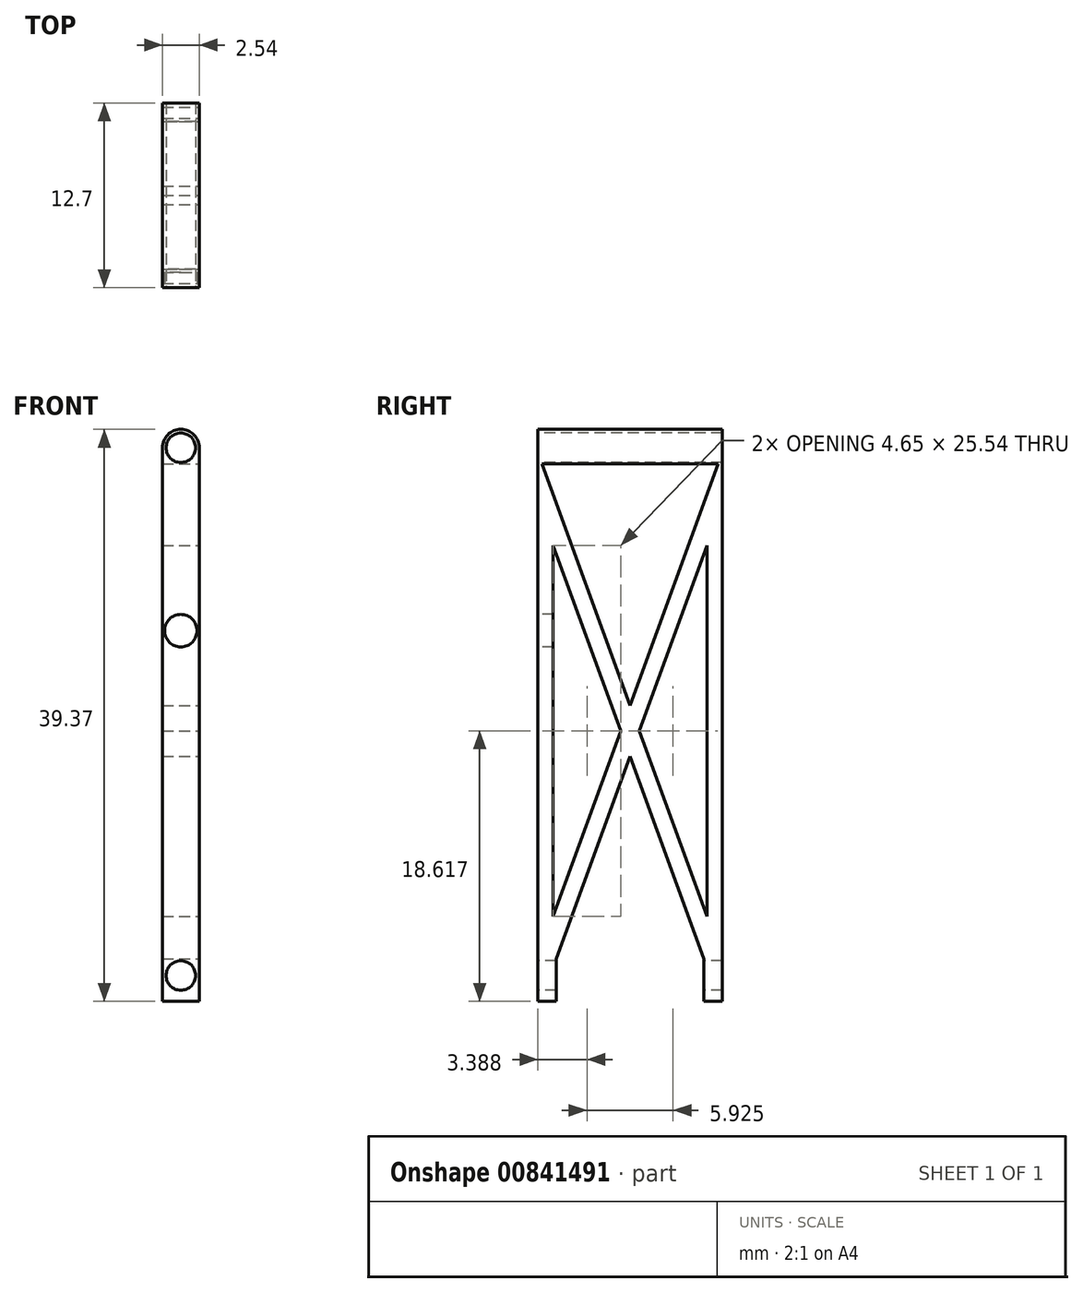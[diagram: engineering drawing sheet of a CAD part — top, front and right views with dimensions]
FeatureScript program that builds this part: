
annotation { "Feature Type Name" : "Feature", "Feature Type Description" : "" }
export const myFeature = defineFeature(function(context is Context, id is Id, definition is map)
    precondition{}
    {
        {
            var Q0;
            Q0=qCreatedBy(makeId("Front.planeOp"),FACE);
            var sketch = newSketch(context, id + "F0", { "sketchPlane" : qUnion([Q0])});
            skArc(sketch, "E0", {"start": v(1.27, 0) * mm, "mid": v(0.9, 0.9) * mm, "end": v(0, 1.27) * mm});
            skArc(sketch, "E1.MirrorCS", {"start": v(-1.27, 0) * mm, "mid": v(-0.9, 0.9) * mm, "end": v(0, 1.27) * mm});
            skLineSegment(sketch, "E2", {"start": v(-1.27, 0) * mm, "end": v(-1.27, -38.1) * mm});
            skLineSegment(sketch, "E3", {"start": v(1.27, 0) * mm, "end": v(1.27, -38.1) * mm});
            skLineSegment(sketch, "E4", {"start": v(-1.27, -38.1) * mm, "end": v(1.27, -38.1) * mm});
            skSolve(sketch);
        }
        {
            var Q0;
            Q0 = qSketchRegion(id + "F0", true);
            extrude(context, id + "F1", {"entities" : qUnion([Q0]), "endBound" : BoundingType.SYMMETRIC, "depth" : 12.7 * mm, "offsetDistance" : 25.4 * mm});
        }
        {
            var Q0;
            Q0=makeQuery(id+"F1.opExtrude","SWEPT_FACE",FACE,{"disambiguationData":[OSD([sQuery(id+"F0.wireOp",EDGE,"E3")])]});
            var sketch = newSketch(context, id + "F2", { "sketchPlane" : qUnion([Q0])});
            skLineSegment(sketch, "E5", {"start": v(-6.35, -0.32) * mm, "end": v(6.35, -35.16) * mm});
            skLineSegment(sketch, "E6", {"start": v(6.35, -0.32) * mm, "end": v(-6.35, -35.16) * mm});
            skLineSegment(sketch, "E7", {"start": v(-5.08, -35.16) * mm, "end": v(6.35, -3.8) * mm});
            skLineSegment(sketch, "E8", {"start": v(-6.35, -3.8) * mm, "end": v(5.08, -35.16) * mm});
            skLineSegment(sketch, "E9", {"start": v(-5.29, -32.25) * mm, "end": v(-5.29, -6.71) * mm});
            skLineSegment(sketch, "E10", {"start": v(5.29, -32.25) * mm, "end": v(5.29, -6.71) * mm});
            skLineSegment(sketch, "E11", {"start": v(-6.35, -35.16) * mm, "end": v(6.35, -35.16) * mm});
            skLineSegment(sketch, "E12", {"start": v(-6.07, -1.1) * mm, "end": v(6.07, -1.1) * mm});
            skSolve(sketch);
        }
        {
            var Q0;
            {var subQ0=sQuery(id+"F2.wireOp",EDGE,"aixSKqG3-rG8t-p5fn-6gs1-k01HcvwCwjLQ");Q0=makeQuery(id+"F2.imprint","IMPRINT",FACE,{"disambiguationData":[TD([[makeQuery(id+"F2.imprint","IMPRINT",EDGE,{"derivedFrom":subQ0}),1.0]])]});}
            var Q1;
            {var subQ0=sQuery(id+"F2.wireOp",EDGE,"E9");Q1=makeQuery(id+"F2.imprint","IMPRINT",FACE,{"disambiguationData":[TD([[makeQuery(id+"F2.imprint","IMPRINT",EDGE,{"derivedFrom":subQ0}),-1.0]])]});}
            var Q2;
            {var subQ0=sQuery(id+"F2.wireOp",EDGE,"E10");Q2=makeQuery(id+"F2.imprint","IMPRINT",FACE,{"disambiguationData":[TD([[makeQuery(id+"F2.imprint","IMPRINT",EDGE,{"derivedFrom":subQ0}),1.0]])]});}
            var Q3;
            {var subQ0=sQuery(id+"F2.wireOp",EDGE,"E11");var subQ1=sQuery(id+"F2.wireOp",EDGE,"E7");var subQ2=makeQuery(id+"F2.imprint","INTERSECT",VERTEX,{"derivedFrom":[subQ1,subQ0]});Q3=makeQuery(id+"F2.imprint","IMPRINT",FACE,{"disambiguationData":[TD([[makeQuery(id+"F2.imprint","IMPRINT",EDGE,{"disambiguationData":[TD([[subQ2,-1.0]])],"derivedFrom":subQ1}),-1.0]])]});}
            var Q4;
            {var subQ0=sQuery(id+"F2.wireOp",EDGE,"E12");Q4=makeQuery(id+"F2.imprint","IMPRINT",FACE,{"disambiguationData":[TD([[makeQuery(id+"F2.imprint","IMPRINT",EDGE,{"derivedFrom":subQ0}),-1.0]])]});}
            extrude(context, id + "F3", {"entities" : qUnion([Q0, Q1, Q2, Q3, Q4]), "operationType" : NewBodyOperationType.REMOVE, "oppositeDirection" : true, "depth" : 2.54 * mm, "offsetDistance" : 25.4 * mm});
        }
        {
            var Q0;
            {var subQ11=sQuery(id+"F0.wireOp",EDGE,"E3");var subQ13=sQuery(id+"F0.wireOp",EDGE,"E4");Q0=makeQuery(id+"F3.boolean.opBoolean","SPLIT",FACE,{"disambiguationData":[TD([makeQuery(id+"F1.opExtrude","SWEPT_FACE",FACE,{"disambiguationData":[OSD([subQ13])]})])],"derivedFrom":makeQuery(id+"F1.opExtrude","SWEPT_FACE",FACE,{"disambiguationData":[OSD([subQ11])]})});}
            var sketch = newSketch(context, id + "F4", { "sketchPlane" : qUnion([Q0])});
            skLineSegment(sketch, "E13", {"start": v(5.08, -35.16) * mm, "end": v(5.08, -38.1) * mm});
            skLineSegment(sketch, "E14", {"start": v(-5.08, -35.16) * mm, "end": v(-5.08, -38.1) * mm});
            skLineSegment(sketch, "E15", {"start": v(-5.08, -35.16) * mm, "end": v(5.08, -35.16) * mm});
            skLineSegment(sketch, "E16", {"start": v(-5.08, -38.1) * mm, "end": v(5.08, -38.1) * mm});
            skSolve(sketch);
        }
        {
            var Q0;
            Q0 = qSketchRegion(id + "F4", true);
            extrude(context, id + "F5", {"entities" : qUnion([Q0]), "operationType" : NewBodyOperationType.REMOVE, "oppositeDirection" : true, "depth" : 2.54 * mm, "offsetDistance" : 25.4 * mm});
        }
        {
            var Q0;
            Q0=makeQuery(id+"F1.opExtrude","CAP_FACE",FACE,{"disambiguationData":[OSD([sQuery(id+"F0.wireOp",EDGE,"E0"),sQuery(id+"F0.wireOp",EDGE,"E1.MirrorCS"),sQuery(id+"F0.wireOp",EDGE,"E2"),sQuery(id+"F0.wireOp",EDGE,"E3"),sQuery(id+"F0.wireOp",EDGE,"E4")])],"isStart":false});
            var sketch = newSketch(context, id + "F6", { "sketchPlane" : qUnion([Q0])});
            skCircle(sketch, "E17", {"center": v(0, -36.32) * mm, "radius": 1.02 * mm});
            skCircle(sketch, "E18", {"center": v(0, 0) * mm, "radius": 1.02 * mm});
            skSolve(sketch);
        }
        {
            var Q0;
            Q0 = qSketchRegion(id + "F6", true);
            extrude(context, id + "F7", {"entities" : qUnion([Q0]), "operationType" : NewBodyOperationType.REMOVE, "oppositeDirection" : true, "depth" : 12.7 * mm, "offsetDistance" : 25.4 * mm});
        }
        {
            var Q0;
            Q0=makeQuery(id+"F1.opExtrude","CAP_FACE",FACE,{"disambiguationData":[OSD([sQuery(id+"F0.wireOp",EDGE,"E0"),sQuery(id+"F0.wireOp",EDGE,"E1.MirrorCS"),sQuery(id+"F0.wireOp",EDGE,"E2"),sQuery(id+"F0.wireOp",EDGE,"E3"),sQuery(id+"F0.wireOp",EDGE,"E4")])],"isStart":false});
            var sketch = newSketch(context, id + "F8", { "sketchPlane" : qUnion([Q0])});
            skCircle(sketch, "E19", {"center": v(0, -12.59) * mm, "radius": 1.12 * mm});
            skSolve(sketch);
        }
        {
            var Q0;
            Q0 = qSketchRegion(id + "F8", true);
            extrude(context, id + "F9", {"entities" : qUnion([Q0]), "operationType" : NewBodyOperationType.REMOVE, "oppositeDirection" : true, "depth" : 2.54 * mm, "offsetDistance" : 25.4 * mm});
        }
    });
